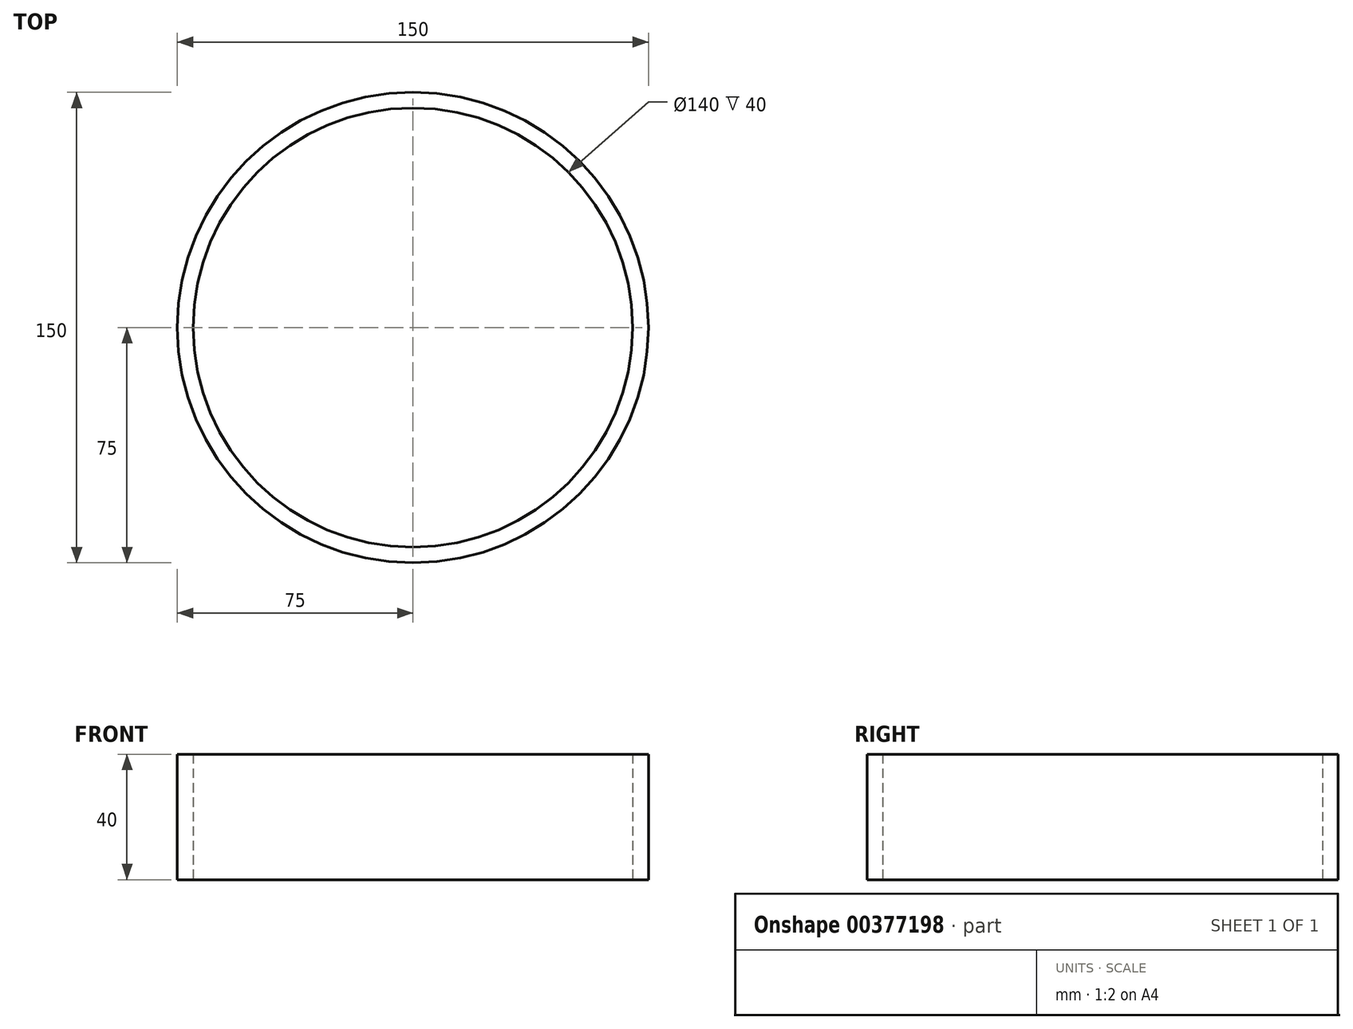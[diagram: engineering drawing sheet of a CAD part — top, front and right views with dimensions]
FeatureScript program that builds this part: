
annotation { "Feature Type Name" : "Feature", "Feature Type Description" : "" }
export const myFeature = defineFeature(function(context is Context, id is Id, definition is map)
    precondition{}
    {
        {
            var Q0;
            Q0=qCreatedBy(makeId("Top.planeOp"),FACE);
            var sketch = newSketch(context, id + "F0", { "sketchPlane" : qUnion([Q0])});
            skCircle(sketch, "E0", {"center": v(0, 0) * mm, "radius": 75 * mm});
            skCircle(sketch, "E1", {"center": v(0, 0) * mm, "radius": 70 * mm});
            skSolve(sketch);
        }
        {
            var Q0;
            Q0 = qSketchRegion(id + "F0", true);
            extrude(context, id + "F1", {"entities" : qUnion([Q0]), "depth" : 40 * mm});
        }
    });
